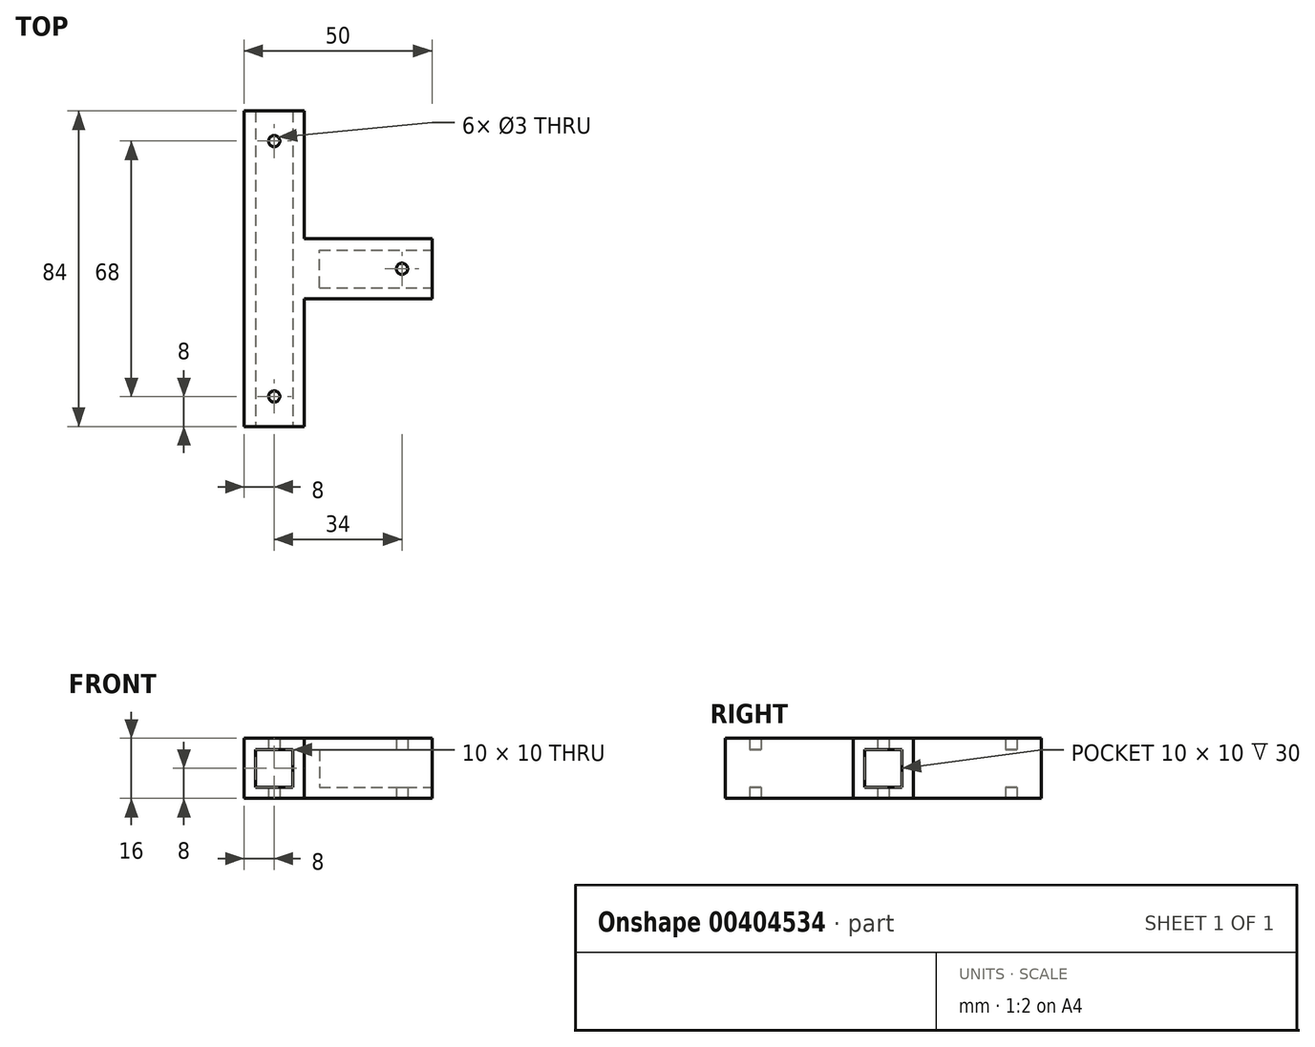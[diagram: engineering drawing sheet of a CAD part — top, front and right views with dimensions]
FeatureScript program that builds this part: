
annotation { "Feature Type Name" : "Feature", "Feature Type Description" : "" }
export const myFeature = defineFeature(function(context is Context, id is Id, definition is map)
    precondition{}
    {
        {
            var Q0;
            Q0=qCreatedBy(makeId("Top.planeOp"),FACE);
            var sketch = newSketch(context, id + "F0", { "sketchPlane" : qUnion([Q0])});
            skLineSegment(sketch, "E0.bottom", {"start": v(-25, 16) * mm, "end": v(25, 16) * mm});
            skLineSegment(sketch, "E0.top", {"start": v(-25, 0) * mm, "end": v(25, 0) * mm});
            skLineSegment(sketch, "E0.left", {"start": v(-25, 16) * mm, "end": v(-25, 0) * mm});
            skLineSegment(sketch, "E0.right", {"start": v(25, 16) * mm, "end": v(25, 0) * mm});
            skLineSegment(sketch, "E1.bottom", {"start": v(-25, 0) * mm, "end": v(-9, 0) * mm});
            skLineSegment(sketch, "E1.top", {"start": v(-25, -34) * mm, "end": v(-9, -34) * mm});
            skLineSegment(sketch, "E1.left", {"start": v(-25, 0) * mm, "end": v(-25, -34) * mm});
            skLineSegment(sketch, "E1.right", {"start": v(-9, 0) * mm, "end": v(-9, -34) * mm});
            skLineSegment(sketch, "E2.bottom", {"start": v(-25, 50) * mm, "end": v(-9, 50) * mm});
            skLineSegment(sketch, "E2.top", {"start": v(-25, 16) * mm, "end": v(-9, 16) * mm});
            skLineSegment(sketch, "E2.left", {"start": v(-25, 50) * mm, "end": v(-25, 16) * mm});
            skLineSegment(sketch, "E2.right", {"start": v(-9, 50) * mm, "end": v(-9, 16) * mm});
            skSolve(sketch);
        }
        {
            var Q0;
            Q0=qSketchRegion(id+"F0",true);
            extrude(context, id + "F1", {"entities" : qUnion([Q0]), "depth" : 16 * mm});
        }
        {
            var Q0;
            Q0=makeQuery(id+"F1.opExtrude","SWEPT_FACE",FACE,{"disambiguationData":[OSD([sQuery(id+"F0.wireOp",EDGE,"E0.right")])]});
            var sketch = newSketch(context, id + "F2", { "sketchPlane" : qUnion([Q0])});
            skLineSegment(sketch, "E3.bottom", {"start": v(3, 13) * mm, "end": v(13, 13) * mm});
            skLineSegment(sketch, "E3.top", {"start": v(3, 3) * mm, "end": v(13, 3) * mm});
            skLineSegment(sketch, "E3.left", {"start": v(3, 13) * mm, "end": v(3, 3) * mm});
            skLineSegment(sketch, "E3.right", {"start": v(13, 13) * mm, "end": v(13, 3) * mm});
            skSolve(sketch);
        }
        {
            var Q0;
            Q0=qSketchRegion(id+"F2",true);
            extrude(context, id + "F3", {"entities" : qUnion([Q0]), "operationType" : NewBodyOperationType.REMOVE, "oppositeDirection" : true, "depth" : 30 * mm});
        }
        {
            var Q0;
            Q0=makeQuery(id+"F1.opExtrude","SWEPT_FACE",FACE,{"disambiguationData":[OSD([sQuery(id+"F0.wireOp",EDGE,"E1.top")])]});
            var sketch = newSketch(context, id + "F4", { "sketchPlane" : qUnion([Q0])});
            skLineSegment(sketch, "E4.bottom", {"start": v(-22, 13) * mm, "end": v(-12, 13) * mm});
            skLineSegment(sketch, "E4.top", {"start": v(-22, 3) * mm, "end": v(-12, 3) * mm});
            skLineSegment(sketch, "E4.left", {"start": v(-22, 13) * mm, "end": v(-22, 3) * mm});
            skLineSegment(sketch, "E4.right", {"start": v(-12, 13) * mm, "end": v(-12, 3) * mm});
            skSolve(sketch);
        }
        {
            var Q0;
            Q0=qSketchRegion(id+"F4",true);
            extrude(context, id + "F5", {"entities" : qUnion([Q0]), "operationType" : NewBodyOperationType.REMOVE, "oppositeDirection" : true, "depth" : 84 * mm});
        }
        {
            var Q0;
            Q0=makeQuery(id+"F1.opExtrude","CAP_FACE",FACE,{"disambiguationData":[OSD([sQuery(id+"F0.wireOp",EDGE,"E0.bottom"),sQuery(id+"F0.wireOp",EDGE,"E0.top"),sQuery(id+"F0.wireOp",EDGE,"E0.left"),sQuery(id+"F0.wireOp",EDGE,"E0.right"),sQuery(id+"F0.wireOp",EDGE,"E1.top"),sQuery(id+"F0.wireOp",EDGE,"E1.left"),sQuery(id+"F0.wireOp",EDGE,"E1.right"),sQuery(id+"F0.wireOp",EDGE,"E2.bottom"),sQuery(id+"F0.wireOp",EDGE,"E2.left"),sQuery(id+"F0.wireOp",EDGE,"E2.right")])],"isStart":true});
            var sketch = newSketch(context, id + "F6", { "sketchPlane" : qUnion([Q0])});
            skCircle(sketch, "E5", {"center": v(-17, -42) * mm, "radius": 1.5 * mm});
            skCircle(sketch, "E6", {"center": v(17, -8) * mm, "radius": 1.5 * mm});
            skCircle(sketch, "E7", {"center": v(-17, 26) * mm, "radius": 1.5 * mm});
            skSolve(sketch);
        }
        {
            var Q0;
            Q0 = qSketchRegion(id + "F6", true);
            extrude(context, id + "F7", {"entities" : qUnion([Q0]), "operationType" : NewBodyOperationType.REMOVE, "oppositeDirection" : true, "depth" : 16 * mm});
        }
    });
